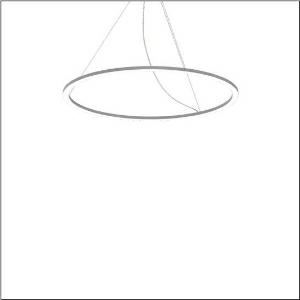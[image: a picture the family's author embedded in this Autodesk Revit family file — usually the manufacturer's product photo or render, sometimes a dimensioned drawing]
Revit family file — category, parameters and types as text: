
# Revit family: silica_r__21_ring-d_5pjbd3d3204a_b808
name_source: partatom
category: Lighting Fixtures
units: mm (PartAtom-declared; Revit-internal decimal feet)

## family parameters
Cut with Voids When Loaded = No
Host = Face
Light Source = No
Part Type = Normal
Room Calculation Point = No
Round Connector Dimension = Use Diameter
Shared = No

## types (1)
- Silica® 21 Ring-D (1 x LED, 8420 lm, 94 W, 4000K)
    Apparent Load = 94 VA
    CIE Flux Codes = 37 69 92 100 100
    Color Rendering = 80
    Color Temperature = 4000K
    Default Elevation = 1800 mm
    Description = Silica® 21 Ring-D, suspended luminaire, of PMMA, frosted, light emission: ring underside luminous distribution, primary light characteristic: symmetric, installation type: suspended mounting, LED, rated luminous flux: 8.420lm, luminous efficacy: 90lm/W, light colour: 840, colour temperature: 4000K, control gear: DALI 2, with terminal, 5-pole, mains connection: 230V, AC/DC, 0/50..60Hz, rated input power: 94W, housing, of extruded aluminium section, metallic grey (RAL 9006), diameter: 1.100mm, ceiling canopy, metallic grey (RAL 9006), protection rating (lamp compartment): IP40, insulation class (complete): insulation class I (protective earthing), certification: CE, impact resistance: IK02, permissible operating ambient temperature: 0..+35°C, packaging unit: 1 piece
    Height = 25 mm  [stored 0.082021 ft]
    Lamp = 1 x LED
    Lamp Light Flux = 8420 lm
    Lamp Power = 94 W
    Lamp count = 1
    Length = 1100 mm
    Luminous efficacy = 90 lm/W
    Manufacturer = Siteco
    ModVariant = No
    Model = 5PJBD3D3204A
    Mounting Place = Ceiling
    Mounting Type = Pendant
    Number of Poles = 1
    OnlyDefault = Yes
    Power Factor = 1
    Product Name = Silica® 21 Ring-D
    Product group = suspended luminaire
    ProductGroupID = 905
    Protection Class = Protection class I
    Protection Degree = IP 40
    RLX_Detail_Level = 1
    RLX_Emergency_Light_Flux = 0 lm
    RLX_Emergency_Type = 0
    RLX_Emergency_Type_DB = No
    RlxData = <blob elided: 14581 chars, md5=a6e725d3>
    Socket = socket
    Standby Power = 0 W
    System Light Flux = 8420 lm
    System Power = 94 W
    Type Comments = Product without accessories
    Type Image = l_1251746.jpg
    URL = http://relux.com
    VarID = ---
    Voltage = 0 V
    Weight = 0.00 kg
    Width = 0 mm  [stored 0 ft]

note: [stored X ft] marks values corroborated as IEEE doubles in the binary element streams (Revit-internal decimal feet)

## geometry (parser evidence)
native form markers: Blend x4, Sweep x10
no freeform markers — native parametric forms only
